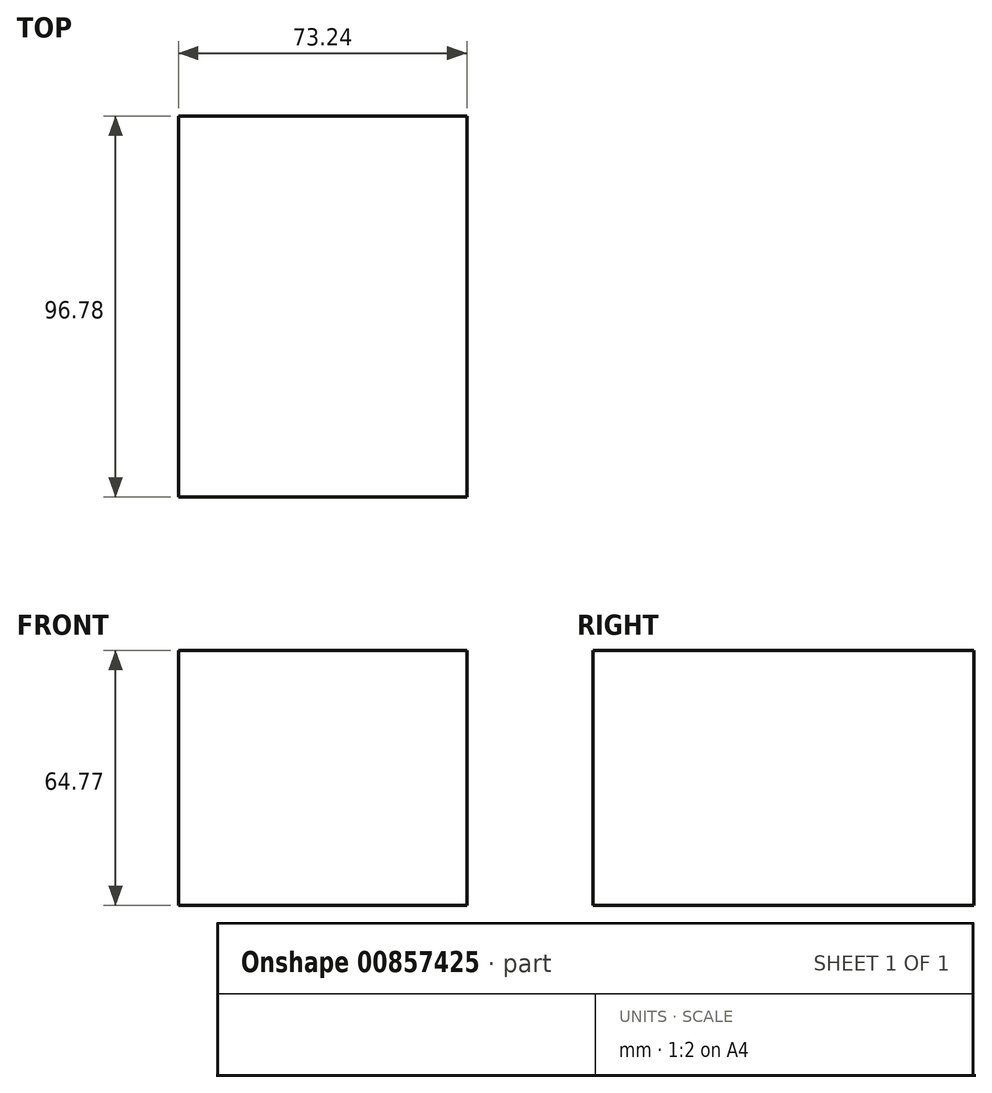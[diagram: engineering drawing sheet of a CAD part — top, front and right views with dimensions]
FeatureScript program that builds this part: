
annotation { "Feature Type Name" : "Feature", "Feature Type Description" : "" }
export const myFeature = defineFeature(function(context is Context, id is Id, definition is map)
    precondition{}
    {
        {
            var Q0;
            Q0=qCreatedBy(makeId("Top.planeOp"),FACE);
            var sketch = newSketch(context, id + "F0", { "sketchPlane" : qUnion([Q0])});
            skLineSegment(sketch, "E0.bottom", {"start": v(40.15, 50.89) * mm, "end": v(-33.1, 50.89) * mm});
            skLineSegment(sketch, "E0.top", {"start": v(40.15, -45.89) * mm, "end": v(-33.1, -45.89) * mm});
            skLineSegment(sketch, "E0.left", {"start": v(40.15, 50.89) * mm, "end": v(40.15, -45.89) * mm});
            skLineSegment(sketch, "E0.right", {"start": v(-33.1, 50.89) * mm, "end": v(-33.1, -45.89) * mm});
            skSolve(sketch);
        }
        {
            var Q0;
            Q0 = qSketchRegion(id + "F0", true);
            extrude(context, id + "F1", {"entities" : qUnion([Q0]), "depth" : 64.77 * mm, "offsetDistance" : 25.4 * mm});
        }
    });
